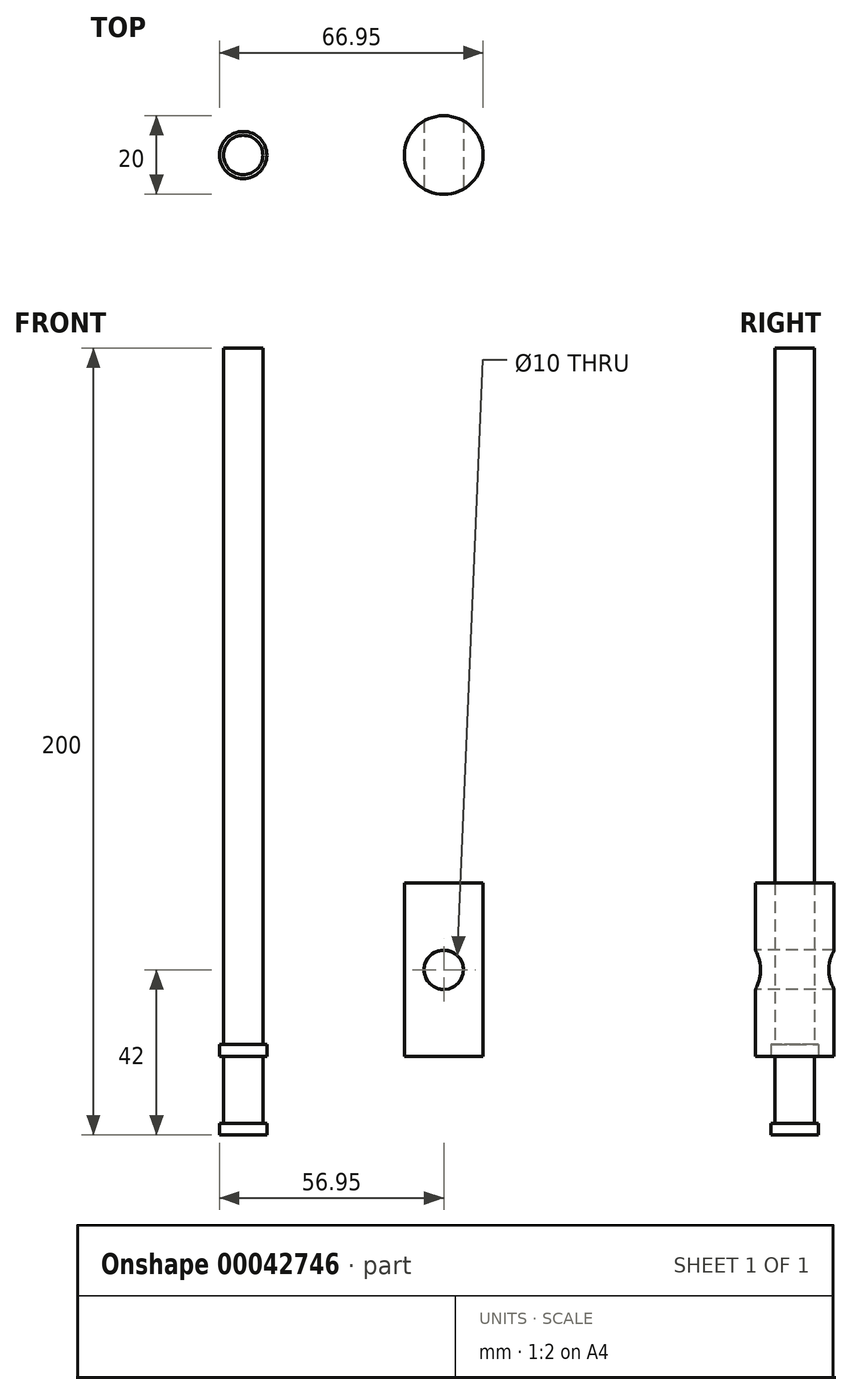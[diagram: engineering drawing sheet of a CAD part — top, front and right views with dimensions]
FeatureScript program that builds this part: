
annotation { "Feature Type Name" : "Feature", "Feature Type Description" : "" }
export const myFeature = defineFeature(function(context is Context, id is Id, definition is map)
    precondition{}
    {
        {
            var Q0;
            Q0=qCreatedBy(makeId("Top.planeOp"),FACE);
            var sketch = newSketch(context, id + "F0", { "sketchPlane" : qUnion([Q0])});
            skCircle(sketch, "E0", {"center": v(0, 0) * mm, "radius": 10 * mm});
            skSolve(sketch);
        }
        {
            var Q0;
            Q0=makeQuery(id+"F0.imprint","IMPRINT",FACE,{"disambiguationData":[TD([[makeQuery(id+"F0.imprint","IMPRINT",EDGE,{"derivedFrom":sQuery(id+"F0.wireOp",EDGE,"E0")}),1.0]])]});
            extrude(context, id + "F1", {"entities" : qUnion([Q0]), "depth" : 44 * mm});
        }
        {
            var Q0;
            Q0=qCreatedBy(makeId("Front.planeOp"),FACE);
            var sketch = newSketch(context, id + "F2", { "sketchPlane" : qUnion([Q0])});
            skCircle(sketch, "E1", {"center": v(0, 22) * mm, "radius": 5 * mm});
            skSolve(sketch);
        }
        {
            var Q0;
            Q0 = qSketchRegion(id + "F2", true);
            extrude(context, id + "F3", {"entities" : qUnion([Q0]), "operationType" : NewBodyOperationType.REMOVE, "oppositeDirection" : true, "depth" : 25 * mm, "hasSecondDirection" : true, "secondDirectionOppositeDirection" : false, "secondDirectionDepth" : 21.06 * mm});
        }
        {
            var Q0;
            Q0=qCreatedBy(makeId("Top.planeOp"),FACE);
            var sketch = newSketch(context, id + "F4", { "sketchPlane" : qUnion([Q0])});
            skCircle(sketch, "E2", {"center": v(-50.95, 0) * mm, "radius": 6 * mm});
            skCircle(sketch, "E3", {"center": v(-50.95, 0) * mm, "radius": 5 * mm});
            skSolve(sketch);
        }
        {
            var Q0;
            Q0 = qSketchRegion(id + "F4", true);
            var Q1;
            Q1=makeQuery(id+"F4.imprint","IMPRINT",FACE,{"disambiguationData":[TD([[makeQuery(id+"F4.imprint","IMPRINT",EDGE,{"derivedFrom":sQuery(id+"F4.wireOp",EDGE,"E3")}),1.0]])]});
            extrude(context, id + "F5", {"entities" : qUnion([Q0, Q1]), "depth" : 3 * mm});
        }
        {
            var Q0;
            Q0=makeQuery(id+"F4.imprint","IMPRINT",FACE,{"disambiguationData":[TD([[makeQuery(id+"F4.imprint","IMPRINT",EDGE,{"derivedFrom":sQuery(id+"F4.wireOp",EDGE,"E3")}),1.0]])]});
            extrude(context, id + "F6", {"entities" : qUnion([Q0]), "operationType" : NewBodyOperationType.ADD, "depth" : 200 * mm});
        }
        {
            var Q0;
            Q0=makeQuery(id+"F5.opExtrude","SWEPT_BODY",BODY,{"disambiguationData":[OSD([sQuery(id+"F4.wireOp",EDGE,"E2")])]});
            transform(context, id + "F7", {"entities" : qUnion([Q0]), "transformType" : TransformType.TRANSLATION_3D, "dx" : 0 * mm, "dy" : 0 * mm, "dz" : -20 * mm, "makeCopy" : false});
        }
        {
            var Q0;
            Q0=makeQuery(id+"F4.imprint","IMPRINT",FACE,{"disambiguationData":[TD([[makeQuery(id+"F4.imprint","IMPRINT",EDGE,{"derivedFrom":sQuery(id+"F4.wireOp",EDGE,"E2")}),1.0]])]});
            extrude(context, id + "F8", {"entities" : qUnion([Q0]), "operationType" : NewBodyOperationType.ADD, "depth" : 3 * mm});
        }
    });
